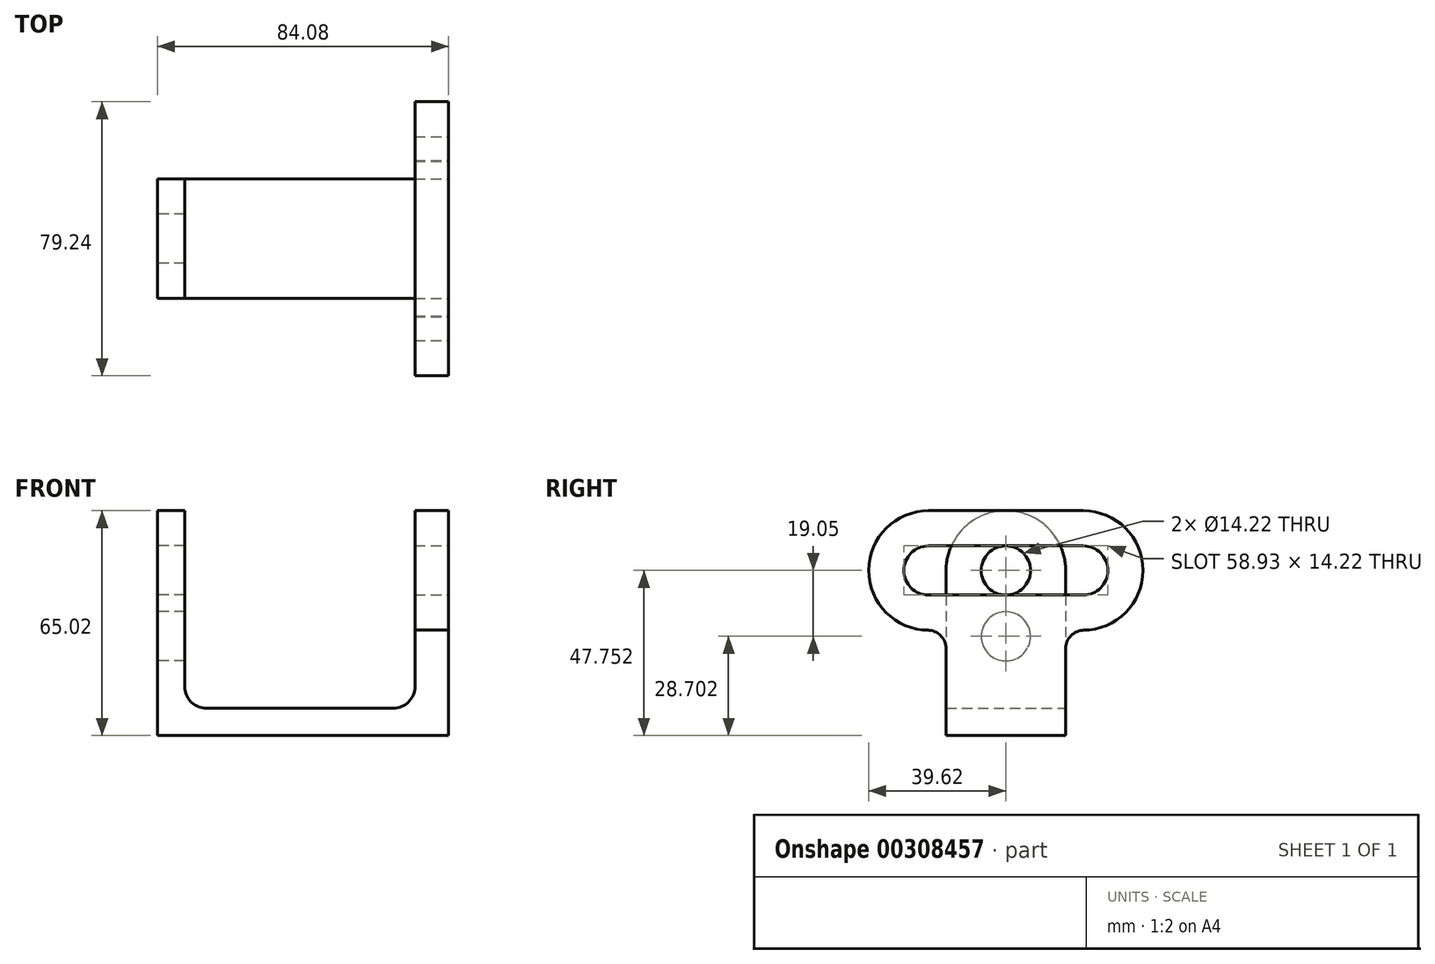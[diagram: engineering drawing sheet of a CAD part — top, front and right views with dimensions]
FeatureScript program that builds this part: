
annotation { "Feature Type Name" : "Feature", "Feature Type Description" : "" }
export const myFeature = defineFeature(function(context is Context, id is Id, definition is map)
    precondition{}
    {
        {
            var Q0;
            Q0=qCreatedBy(makeId("Front.planeOp"),FACE);
            var sketch = newSketch(context, id + "F0", { "sketchPlane" : qUnion([Q0])});
            skLineSegment(sketch, "E0", {"start": v(-42.04, 0) * mm, "end": v(42.04, 0) * mm});
            skLineSegment(sketch, "E1", {"start": v(-42.04, 0) * mm, "end": v(-42.04, 47.75) * mm});
            skLineSegment(sketch, "E2", {"start": v(-42.04, 47.75) * mm, "end": v(-34.16, 47.75) * mm});
            skLineSegment(sketch, "E3", {"start": v(-34.16, 47.75) * mm, "end": v(-34.16, 7.87) * mm});
            skLineSegment(sketch, "E4", {"start": v(-34.16, 7.87) * mm, "end": v(32.39, 7.87) * mm});
            skLineSegment(sketch, "E5", {"start": v(32.39, 7.87) * mm, "end": v(32.38, 47.75) * mm});
            skLineSegment(sketch, "E6", {"start": v(32.38, 47.75) * mm, "end": v(42.04, 47.75) * mm});
            skLineSegment(sketch, "E7", {"start": v(42.04, 47.75) * mm, "end": v(42.04, 0) * mm});
            skArc(sketch, "E8", {"start": v(-34.16, 14.22) * mm, "mid": v(-32.3, 9.73) * mm, "end": v(-27.81, 7.87) * mm});
            skArc(sketch, "E9", {"start": v(26.04, 7.87) * mm, "mid": v(30.53, 9.73) * mm, "end": v(32.39, 14.22) * mm});
            skSolve(sketch);
        }
        {
            var Q0;
            Q0=makeQuery(id+"F0.imprint","IMPRINT",FACE,{"disambiguationData":[TD([[makeQuery(id+"F0.imprint","IMPRINT",EDGE,{"derivedFrom":sQuery(id+"F0.wireOp",EDGE,"E0")}),1.0]])]});
            var Q1;
            {var subQ3=sQuery(id+"F0.wireOp",EDGE,"E8");Q1=makeQuery(id+"F0.imprint","IMPRINT",FACE,{"disambiguationData":[TD([[makeQuery(id+"F0.imprint","IMPRINT",EDGE,{"derivedFrom":subQ3}),-1.0]])]});}
            var Q2;
            {var subQ3=sQuery(id+"F0.wireOp",EDGE,"E9");Q2=makeQuery(id+"F0.imprint","IMPRINT",FACE,{"disambiguationData":[TD([[makeQuery(id+"F0.imprint","IMPRINT",EDGE,{"derivedFrom":subQ3}),-1.0]])]});}
            extrude(context, id + "F1", {"entities" : qUnion([Q0, Q1, Q2]), "endBound" : BoundingType.SYMMETRIC, "depth" : 34.54 * mm});
        }
        {
            var Q0;
            Q0=makeQuery(id+"F1.opExtrude","SWEPT_FACE",FACE,{"disambiguationData":[OSD([sQuery(id+"F0.wireOp",EDGE,"E1")])]});
            var sketch = newSketch(context, id + "F2", { "sketchPlane" : qUnion([Q0])});
            skCircle(sketch, "E10", {"center": v(0, 28.7) * mm, "radius": 7.11 * mm});
            skCircle(sketch, "E11", {"center": v(0, 47.75) * mm, "radius": 7.11 * mm});
            skArc(sketch, "E12", {"start": v(17.27, 47.75) * mm, "mid": v(0, 65.02) * mm, "end": v(-17.27, 47.75) * mm});
            skSolve(sketch);
        }
        {
            var Q0;
            {var subQ5=sQuery(id+"F2.wireOp",EDGE,"E12");Q0=makeQuery(id+"F2.imprint","IMPRINT",FACE,{"disambiguationData":[TD([[makeQuery(id+"F2.imprint","IMPRINT",EDGE,{"derivedFrom":subQ5}),1.0]])]});}
            var Q1;
            Q1=makeQuery(id+"F1.opExtrude","SWEPT_FACE",FACE,{"disambiguationData":[OSD([sQuery(id+"F0.wireOp",EDGE,"E3")])]});
            extrude(context, id + "F3", {"entities" : qUnion([Q0]), "operationType" : NewBodyOperationType.ADD, "endBound" : BoundingType.UP_TO_SURFACE, "oppositeDirection" : true, "endBoundEntityFace" : qUnion([Q1]), "depth" : 25.4 * mm});
        }
        {
            var Q0;
            Q0 = qSketchRegion(id + "F2", true);
            var Q1;
            Q1=makeQuery(id+"F1.opExtrude","SWEPT_FACE",FACE,{"disambiguationData":[OSD([sQuery(id+"F0.wireOp",EDGE,"E5")])]});
            extrude(context, id + "F4", {"entities" : qUnion([Q0]), "operationType" : NewBodyOperationType.REMOVE, "endBound" : BoundingType.UP_TO_SURFACE, "oppositeDirection" : true, "endBoundEntityFace" : qUnion([Q1]), "depth" : 25.4 * mm});
        }
        {
            var Q0;
            Q0=makeQuery(id+"F1.opExtrude","SWEPT_FACE",FACE,{"disambiguationData":[OSD([sQuery(id+"F0.wireOp",EDGE,"E7")])]});
            var sketch = newSketch(context, id + "F5", { "sketchPlane" : qUnion([Q0])});
            skLineSegment(sketch, "E13", {"start": v(-22.35, 47.75) * mm, "end": v(22.35, 47.75) * mm, "construction": true});
            skArc(sketch, "E14.0.startCap", {"start": v(-22.35, 30.48) * mm, "mid": v(-39.62, 47.75) * mm, "end": v(-22.35, 65.02) * mm});
            skArc(sketch, "E14.0.endCap", {"start": v(22.35, 65.02) * mm, "mid": v(39.62, 47.75) * mm, "end": v(22.35, 30.48) * mm});
            skLineSegment(sketch, "E14.0.left", {"start": v(-22.35, 65.02) * mm, "end": v(22.35, 65.02) * mm});
            skLineSegment(sketch, "E14.0.right", {"start": v(-22.35, 30.48) * mm, "end": v(22.35, 30.48) * mm});
            skArc(sketch, "E15.0.startCap", {"start": v(-22.35, 40.64) * mm, "mid": v(-29.46, 47.75) * mm, "end": v(-22.35, 54.86) * mm});
            skArc(sketch, "E15.0.endCap", {"start": v(22.35, 54.86) * mm, "mid": v(29.46, 47.75) * mm, "end": v(22.35, 40.64) * mm});
            skLineSegment(sketch, "E15.0.left", {"start": v(-22.35, 54.86) * mm, "end": v(22.35, 54.86) * mm});
            skLineSegment(sketch, "E15.0.right", {"start": v(-22.35, 40.64) * mm, "end": v(22.35, 40.64) * mm});
            skSolve(sketch);
        }
        {
            var Q0;
            Q0 = qSketchRegion(id + "F5", true);
            extrude(context, id + "F6", {"entities" : qUnion([Q0]), "operationType" : NewBodyOperationType.ADD, "oppositeDirection" : true, "depth" : 9.65 * mm});
        }
        {
            var Q0;
            Q0=makeQuery(id+"F6.boolean.opBoolean","MERGE",FACE,{"derivedFrom":[makeQuery(id+"F1.opExtrude","SWEPT_FACE",FACE,{"disambiguationData":[OSD([sQuery(id+"F0.wireOp",EDGE,"E7")])]}),makeQuery(id+"F6.opExtrude","CAP_FACE",FACE,{"disambiguationData":[OSD([sQuery(id+"F5.wireOp",EDGE,"E14.0.startCap"),sQuery(id+"F5.wireOp",EDGE,"E14.0.endCap"),sQuery(id+"F5.wireOp",EDGE,"E14.0.left"),sQuery(id+"F5.wireOp",EDGE,"E14.0.right"),sQuery(id+"F5.wireOp",EDGE,"E15.0.startCap"),sQuery(id+"F5.wireOp",EDGE,"E15.0.endCap"),sQuery(id+"F5.wireOp",EDGE,"E15.0.left"),sQuery(id+"F5.wireOp",EDGE,"E15.0.right")])],"isStart":true})]});
            var sketch = newSketch(context, id + "F7", { "sketchPlane" : qUnion([Q0])});
            skLineSegment(sketch, "E16.bottom", {"start": v(-17.27, 47.75) * mm, "end": v(17.27, 47.75) * mm});
            skLineSegment(sketch, "E16.top", {"start": v(-17.27, 40.64) * mm, "end": v(17.27, 40.64) * mm});
            skLineSegment(sketch, "E16.left", {"start": v(-17.27, 47.75) * mm, "end": v(-17.27, 40.64) * mm});
            skLineSegment(sketch, "E16.right", {"start": v(17.27, 47.75) * mm, "end": v(17.27, 40.64) * mm});
            skSolve(sketch);
        }
        {
            var Q0;
            Q0 = qSketchRegion(id + "F7", true);
            extrude(context, id + "F8", {"entities" : qUnion([Q0]), "operationType" : NewBodyOperationType.REMOVE, "oppositeDirection" : true, "depth" : 9.65 * mm});
        }
        {
            var Q0;
            Q0=makeQuery(id+"F6.boolean.opBoolean","MERGE",FACE,{"derivedFrom":[makeQuery(id+"F1.opExtrude","SWEPT_FACE",FACE,{"disambiguationData":[OSD([sQuery(id+"F0.wireOp",EDGE,"E7")])]}),makeQuery(id+"F6.opExtrude","CAP_FACE",FACE,{"disambiguationData":[OSD([sQuery(id+"F5.wireOp",EDGE,"E14.0.startCap"),sQuery(id+"F5.wireOp",EDGE,"E14.0.endCap"),sQuery(id+"F5.wireOp",EDGE,"E14.0.left"),sQuery(id+"F5.wireOp",EDGE,"E14.0.right"),sQuery(id+"F5.wireOp",EDGE,"E15.0.startCap"),sQuery(id+"F5.wireOp",EDGE,"E15.0.endCap"),sQuery(id+"F5.wireOp",EDGE,"E15.0.left"),sQuery(id+"F5.wireOp",EDGE,"E15.0.right")])],"isStart":true})]});
            var sketch = newSketch(context, id + "F9", { "sketchPlane" : qUnion([Q0])});
            skArc(sketch, "E17", {"start": v(-17.27, 25.15) * mm, "mid": v(-18.83, 28.92) * mm, "end": v(-22.6, 30.48) * mm});
            skArc(sketch, "E18", {"start": v(22.6, 30.48) * mm, "mid": v(18.83, 28.92) * mm, "end": v(17.27, 25.15) * mm});
            skLineSegment(sketch, "E19", {"start": v(-22.6, 30.48) * mm, "end": v(-17.27, 30.48) * mm});
            skLineSegment(sketch, "E20", {"start": v(-17.27, 30.48) * mm, "end": v(-17.27, 25.15) * mm});
            skLineSegment(sketch, "E21", {"start": v(17.27, 25.15) * mm, "end": v(17.27, 30.48) * mm});
            skLineSegment(sketch, "E22", {"start": v(17.27, 30.48) * mm, "end": v(22.6, 30.48) * mm});
            skSolve(sketch);
        }
        {
            var Q0;
            {var subQ0=sQuery(id+"F9.wireOp",EDGE,"E17");Q0=makeQuery(id+"F9.imprint","IMPRINT",FACE,{"disambiguationData":[TD([[makeQuery(id+"F9.imprint","IMPRINT",EDGE,{"derivedFrom":subQ0}),-1.0]])]});}
            var Q1;
            {var subQ0=sQuery(id+"F9.wireOp",EDGE,"E18");Q1=makeQuery(id+"F9.imprint","IMPRINT",FACE,{"disambiguationData":[TD([[makeQuery(id+"F9.imprint","IMPRINT",EDGE,{"derivedFrom":subQ0}),-1.0]])]});}
            extrude(context, id + "F10", {"entities" : qUnion([Q0, Q1]), "operationType" : NewBodyOperationType.ADD, "oppositeDirection" : true, "depth" : 9.65 * mm});
        }
    });
